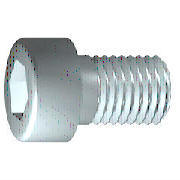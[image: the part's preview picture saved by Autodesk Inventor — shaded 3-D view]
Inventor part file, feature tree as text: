
AUTODESK INVENTOR PART (.ipt)
format: ipt  version: 2013 (Build 170138000, 138)  size: 179,200 bytes
history: native  units: mm (DEFAULTED — no unit token found)
features: sketch x2, extrude x1, plane x1, fillet x1
ambient origin geometry x7: Origin, YZ Plane, XY Plane, X Axis, Y Axis, Z Axis, Center Point
bodies: Solid1 (feature_tree), Body (feature_tree)
feature tree (5):
  extrude  "Slot"  Depth=0.306825mm
  plane  "Work Plane1"
  fillet  "Fillet2"  Radius=3.0mm
  sketch  "Sketch1"  dims[d1=18.0mm d2=0.306825mm d3=3.0mm]
  sketch  "Sketch2"  dims[d4=1.5mm d5=60.0deg d6=3.0mm d7=3.0mm d8=2.886751mm d9=5.5mm d10=90.0deg d11=10.0mm d12=0.0mm d13=18.0mm d14=0.0mm d15=0.306725mm d16=0.306725mm d17=0.3mm d19=0.0mm d26=35.0mm d27=45.0deg d28=0.0mm d29=0.0mm d30=0.1mm]
